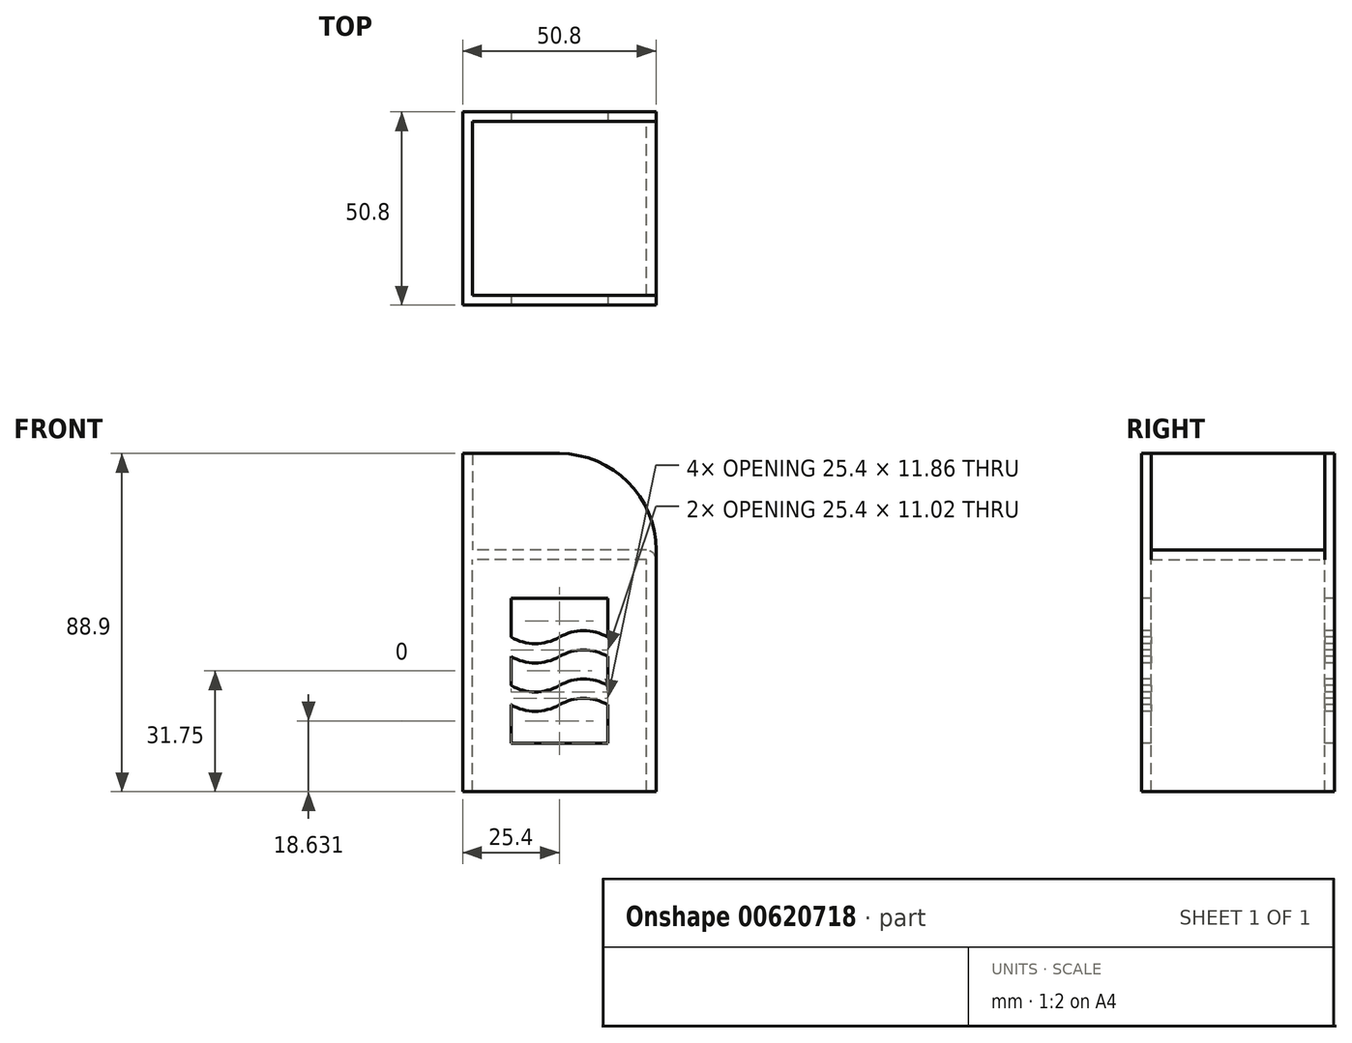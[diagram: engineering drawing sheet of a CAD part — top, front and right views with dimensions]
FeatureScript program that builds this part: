
annotation { "Feature Type Name" : "Feature", "Feature Type Description" : "" }
export const myFeature = defineFeature(function(context is Context, id is Id, definition is map)
    precondition{}
    {
        {
            var Q0;
            Q0=qCreatedBy(makeId("Right.planeOp"),FACE);
            var sketch = newSketch(context, id + "F0", { "sketchPlane" : qUnion([Q0])});
            skLineSegment(sketch, "E0.bottom", {"start": v(-25.4, -31.75) * mm, "end": v(25.4, -31.75) * mm});
            skLineSegment(sketch, "E0.top", {"start": v(-25.4, 31.75) * mm, "end": v(25.4, 31.75) * mm});
            skLineSegment(sketch, "E0.left", {"start": v(-25.4, -31.75) * mm, "end": v(-25.4, 31.75) * mm});
            skLineSegment(sketch, "E0.right", {"start": v(25.4, -31.75) * mm, "end": v(25.4, 31.75) * mm});
            skPoint(sketch, "E0.middle", {"position": v(0, 0) * mm});
            skLineSegment(sketch, "E1.bottom", {"start": v(12.7, -12.7) * mm, "end": v(-12.7, -12.7) * mm});
            skLineSegment(sketch, "E1.top", {"start": v(12.7, 25.4) * mm, "end": v(-12.7, 25.4) * mm});
            skLineSegment(sketch, "E1.left", {"start": v(12.7, -12.7) * mm, "end": v(12.7, 25.4) * mm});
            skLineSegment(sketch, "E1.right", {"start": v(-12.7, -12.7) * mm, "end": v(-12.7, 25.4) * mm});
            skPoint(sketch, "E1.middle", {"position": v(0, 6.35) * mm});
            skArc(sketch, "E2", {"start": v(-12.7, 15.24) * mm, "mid": v(-6.35, 13.54) * mm, "end": v(0, 15.24) * mm});
            skArc(sketch, "E3", {"start": v(12.7, 15.24) * mm, "mid": v(6.35, 16.94) * mm, "end": v(0, 15.24) * mm});
            skArc(sketch, "E4.0.1.0", {"start": v(12.7, 10.16) * mm, "mid": v(6.35, 11.86) * mm, "end": v(0, 10.16) * mm});
            skArc(sketch, "E4.0.1.1", {"start": v(-12.7, 10.16) * mm, "mid": v(-6.35, 8.46) * mm, "end": v(0, 10.16) * mm});
            skLineSegment(sketch, "E4.direction1", {"start": v(0, 15.24) * mm, "end": v(25.33, 15.24) * mm, "construction": true});
            skLineSegment(sketch, "E4.direction2", {"start": v(0, 15.24) * mm, "end": v(0, 10.16) * mm, "construction": true});
            skArc(sketch, "E5.0.1.0", {"start": v(12.7, -2.54) * mm, "mid": v(6.35, -0.84) * mm, "end": v(0, -2.54) * mm});
            skArc(sketch, "E5.0.1.1", {"start": v(12.7, 2.54) * mm, "mid": v(6.35, 4.24) * mm, "end": v(0, 2.54) * mm});
            skArc(sketch, "E5.0.1.2", {"start": v(-12.7, -2.54) * mm, "mid": v(-6.35, -4.24) * mm, "end": v(0, -2.54) * mm});
            skArc(sketch, "E5.0.1.3", {"start": v(-12.7, 2.54) * mm, "mid": v(-6.35, 0.84) * mm, "end": v(0, 2.54) * mm});
            skLineSegment(sketch, "E5.direction1", {"start": v(0, 10.16) * mm, "end": v(25.33, 10.16) * mm, "construction": true});
            skLineSegment(sketch, "E5.direction2", {"start": v(0, 10.16) * mm, "end": v(0, -2.54) * mm, "construction": true});
            skSolve(sketch);
        }
        {
            var Q0;
            {var subQ1=sQuery(id+"F0.wireOp",EDGE,"E2");Q0=makeQuery(id+"F0.imprint","IMPRINT",FACE,{"disambiguationData":[TD([[makeQuery(id+"F0.imprint","IMPRINT",EDGE,{"derivedFrom":subQ1}),-1.0]])]});}
            var Q1;
            {var subQ1=sQuery(id+"F0.wireOp",EDGE,"E5.0.1.0");Q1=makeQuery(id+"F0.imprint","IMPRINT",FACE,{"disambiguationData":[TD([[makeQuery(id+"F0.imprint","IMPRINT",EDGE,{"derivedFrom":subQ1}),-1.0]])]});}
            var Q2;
            {var subQ1=sQuery(id+"F0.wireOp",EDGE,"E4.0.1.0");Q2=makeQuery(id+"F0.imprint","IMPRINT",FACE,{"disambiguationData":[TD([[makeQuery(id+"F0.imprint","IMPRINT",EDGE,{"derivedFrom":subQ1}),1.0]])]});}
            var Q3;
            {var subQ2=sQuery(id+"F0.wireOp",EDGE,"E1.bottom");Q3=makeQuery(id+"F0.imprint","IMPRINT",FACE,{"disambiguationData":[TD([[makeQuery(id+"F0.imprint","IMPRINT",EDGE,{"derivedFrom":subQ2}),-1.0]])]});}
            var Q4;
            {var subQ1=sQuery(id+"F0.wireOp",EDGE,"E1.top");Q4=makeQuery(id+"F0.imprint","IMPRINT",FACE,{"disambiguationData":[TD([[makeQuery(id+"F0.imprint","IMPRINT",EDGE,{"derivedFrom":subQ1}),1.0]])]});}
            var Q5;
            Q5=makeQuery(id+"F0.imprint","IMPRINT",FACE,{"disambiguationData":[TD([[makeQuery(id+"F0.imprint","IMPRINT",EDGE,{"derivedFrom":sQuery(id+"F0.wireOp",EDGE,"E0.bottom")}),1.0]])]});
            extrude(context, id + "F1", {"entities" : qUnion([Q0, Q1, Q2, Q3, Q4, Q5]), "endBound" : BoundingType.SYMMETRIC, "depth" : 50.8 * mm, "offsetDistance" : 25.4 * mm});
        }
        {
            var Q0;
            Q0=makeQuery(id+"F1.opExtrude","SWEPT_FACE",FACE,{"disambiguationData":[OSD([sQuery(id+"F0.wireOp",EDGE,"E0.bottom")])]});
            shell(context, id + "F2", {"entities" : qUnion([Q0]), "thickness" : 2.54 * mm});
        }
        {
            var Q0;
            Q0=makeQuery(id+"F1.opExtrude","SWEPT_FACE",FACE,{"disambiguationData":[OSD([sQuery(id+"F0.wireOp",EDGE,"E0.top")])]});
            var sketch = newSketch(context, id + "F3", { "sketchPlane" : qUnion([Q0])});
            skLineSegment(sketch, "E6.bottom", {"start": v(25.4, -22.86) * mm, "end": v(-22.86, -22.86) * mm});
            skLineSegment(sketch, "E6.top", {"start": v(25.4, 22.86) * mm, "end": v(-22.86, 22.86) * mm});
            skLineSegment(sketch, "E6.left", {"start": v(25.4, -22.86) * mm, "end": v(25.4, 22.86) * mm});
            skLineSegment(sketch, "E6.right", {"start": v(-22.86, -22.86) * mm, "end": v(-22.86, 22.86) * mm});
            skSolve(sketch);
        }
        {
            var Q0;
            {var subQ3=sQuery(id+"F3.wireOp",EDGE,"E6.bottom");Q0=makeQuery(id+"F3.imprint","IMPRINT",FACE,{"disambiguationData":[TD([[makeQuery(id+"F3.imprint","IMPRINT",EDGE,{"derivedFrom":subQ3}),1.0]])]});}
            extrude(context, id + "F4", {"entities" : qUnion([Q0]), "operationType" : NewBodyOperationType.ADD, "depth" : 25.4 * mm, "offsetDistance" : 25.4 * mm});
        }
        {
            var Q0;
            {var subQ0=sQuery(id+"F0.wireOp",EDGE,"E0.top");var subQ1=makeQuery(id+"F1.opExtrude","CAP_EDGE",EDGE,{"disambiguationData":[OSD([subQ0])],"isStart":false});Q0=makeQuery(id+"F4.opExtrude","CAP_EDGE",EDGE,{"disambiguationData":[OSD([subQ0]),TDD([makeQuery(id+"F3.imprint","IMPRINT",EDGE,{"disambiguationData":[TD([[makeQuery(id+"F3.imprint","INTERSECT",VERTEX,{"derivedFrom":[makeQuery(id+"F1.opExtrude","SWEPT_EDGE",EDGE,{"disambiguationData":[OSD([subQ0,sQuery(id+"F0.wireOp",EDGE,"E0.left")])]}),subQ1]}),-1.0]])],"derivedFrom":subQ1})])],"isStart":false});}
            var Q1;
            {var subQ0=sQuery(id+"F0.wireOp",EDGE,"E0.top");var subQ1=makeQuery(id+"F1.opExtrude","CAP_EDGE",EDGE,{"disambiguationData":[OSD([subQ0])],"isStart":false});Q1=makeQuery(id+"F4.opExtrude","CAP_EDGE",EDGE,{"disambiguationData":[OSD([subQ0]),TDD([makeQuery(id+"F3.imprint","IMPRINT",EDGE,{"disambiguationData":[TD([[makeQuery(id+"F3.imprint","INTERSECT",VERTEX,{"derivedFrom":[makeQuery(id+"F1.opExtrude","SWEPT_EDGE",EDGE,{"disambiguationData":[OSD([subQ0,sQuery(id+"F0.wireOp",EDGE,"E0.right")])]}),subQ1]}),1.0]])],"derivedFrom":subQ1})])],"isStart":false});}
            fillet(context, id + "F5", {"entities" : qUnion([Q0, Q1]), "radius" : 25.4 * mm, "tangentPropagation" : true, "allowEdgeOverflow" : false});
        }
        {
            var Q0;
            Q0=makeQuery(id+"F1.opExtrude","CAP_EDGE",EDGE,{"disambiguationData":[OSD([sQuery(id+"F0.wireOp",EDGE,"E0.top")])],"isStart":false});
            fillet(context, id + "F6", {"entities" : qUnion([Q0]), "radius" : 2.54 * mm, "tangentPropagation" : true, "allowEdgeOverflow" : false});
        }
        {
            var Q0;
            {var subQ0=sQuery(id+"F0.wireOp",EDGE,"E0.left");Q0=makeQuery(id+"F4.boolean.opBoolean","MERGE",FACE,{"derivedFrom":[makeQuery(id+"F1.opExtrude","SWEPT_FACE",FACE,{"disambiguationData":[OSD([subQ0])]}),makeQuery(id+"F4.opExtrude","SWEPT_FACE",FACE,{"disambiguationData":[OSD([sQuery(id+"F0.wireOp",EDGE,"E0.top"),subQ0])]})]});}
            var sketch = newSketch(context, id + "F7", { "sketchPlane" : qUnion([Q0])});
            skLineSegment(sketch, "E7.bottom", {"start": v(-12.7, -19.05) * mm, "end": v(12.7, -19.05) * mm});
            skLineSegment(sketch, "E7.top", {"start": v(-12.7, 19.05) * mm, "end": v(12.7, 19.05) * mm});
            skLineSegment(sketch, "E7.left", {"start": v(-12.7, -19.05) * mm, "end": v(-12.7, 19.05) * mm});
            skLineSegment(sketch, "E7.right", {"start": v(12.7, -19.05) * mm, "end": v(12.7, 19.05) * mm});
            skArc(sketch, "E8", {"start": v(-12.7, 3.8) * mm, "mid": v(-6.35, 2.1) * mm, "end": v(0, 3.8) * mm});
            skArc(sketch, "E9", {"start": v(12.7, 3.8) * mm, "mid": v(6.35, 5.51) * mm, "end": v(0, 3.8) * mm});
            skArc(sketch, "E10", {"start": v(-12.7, 8.89) * mm, "mid": v(-6.35, 7.19) * mm, "end": v(0, 8.89) * mm});
            skPoint(sketch, "E10.midSnap0", {"position": v(6.35, 5.51) * mm});
            skPoint(sketch, "E10.midSnap1", {"position": v(-6.35, 2.1) * mm});
            skArc(sketch, "E11", {"start": v(12.7, 8.89) * mm, "mid": v(6.35, 10.6) * mm, "end": v(0, 8.89) * mm});
            skPoint(sketch, "E11.startSnap0", {"position": v(12.7, 0) * mm});
            skArc(sketch, "E12.0.1.0", {"start": v(-12.7, -3.81) * mm, "mid": v(-6.35, -5.51) * mm, "end": v(0, -3.81) * mm});
            skArc(sketch, "E12.0.1.1", {"start": v(-12.7, -8.9) * mm, "mid": v(-6.35, -10.6) * mm, "end": v(0, -8.9) * mm});
            skArc(sketch, "E12.0.1.2", {"start": v(12.7, -8.9) * mm, "mid": v(6.35, -7.19) * mm, "end": v(0, -8.9) * mm});
            skArc(sketch, "E12.0.1.3", {"start": v(12.7, -3.81) * mm, "mid": v(6.35, -2.1) * mm, "end": v(0, -3.81) * mm});
            skLineSegment(sketch, "E12.direction1", {"start": v(-12.7, 8.89) * mm, "end": v(12.7, 8.89) * mm, "construction": true});
            skLineSegment(sketch, "E12.direction2", {"start": v(-12.7, 8.89) * mm, "end": v(-12.7, -3.81) * mm, "construction": true});
            skSolve(sketch);
        }
        {
            var Q0;
            {var subQ2=sQuery(id+"F7.wireOp",EDGE,"E7.top");Q0=makeQuery(id+"F7.imprint","IMPRINT",FACE,{"disambiguationData":[TD([[makeQuery(id+"F7.imprint","IMPRINT",EDGE,{"derivedFrom":subQ2}),-1.0]])]});}
            var Q1;
            {var subQ1=sQuery(id+"F7.wireOp",EDGE,"E8");Q1=makeQuery(id+"F7.imprint","IMPRINT",FACE,{"disambiguationData":[TD([[makeQuery(id+"F7.imprint","IMPRINT",EDGE,{"derivedFrom":subQ1}),-1.0]])]});}
            var Q2;
            {var subQ2=sQuery(id+"F7.wireOp",EDGE,"E7.bottom");Q2=makeQuery(id+"F7.imprint","IMPRINT",FACE,{"disambiguationData":[TD([[makeQuery(id+"F7.imprint","IMPRINT",EDGE,{"derivedFrom":subQ2}),1.0]])]});}
            extrude(context, id + "F8", {"entities" : qUnion([Q0, Q1, Q2]), "operationType" : NewBodyOperationType.REMOVE, "oppositeDirection" : true, "depth" : 50.8 * mm, "offsetDistance" : 25.4 * mm});
        }
    });
